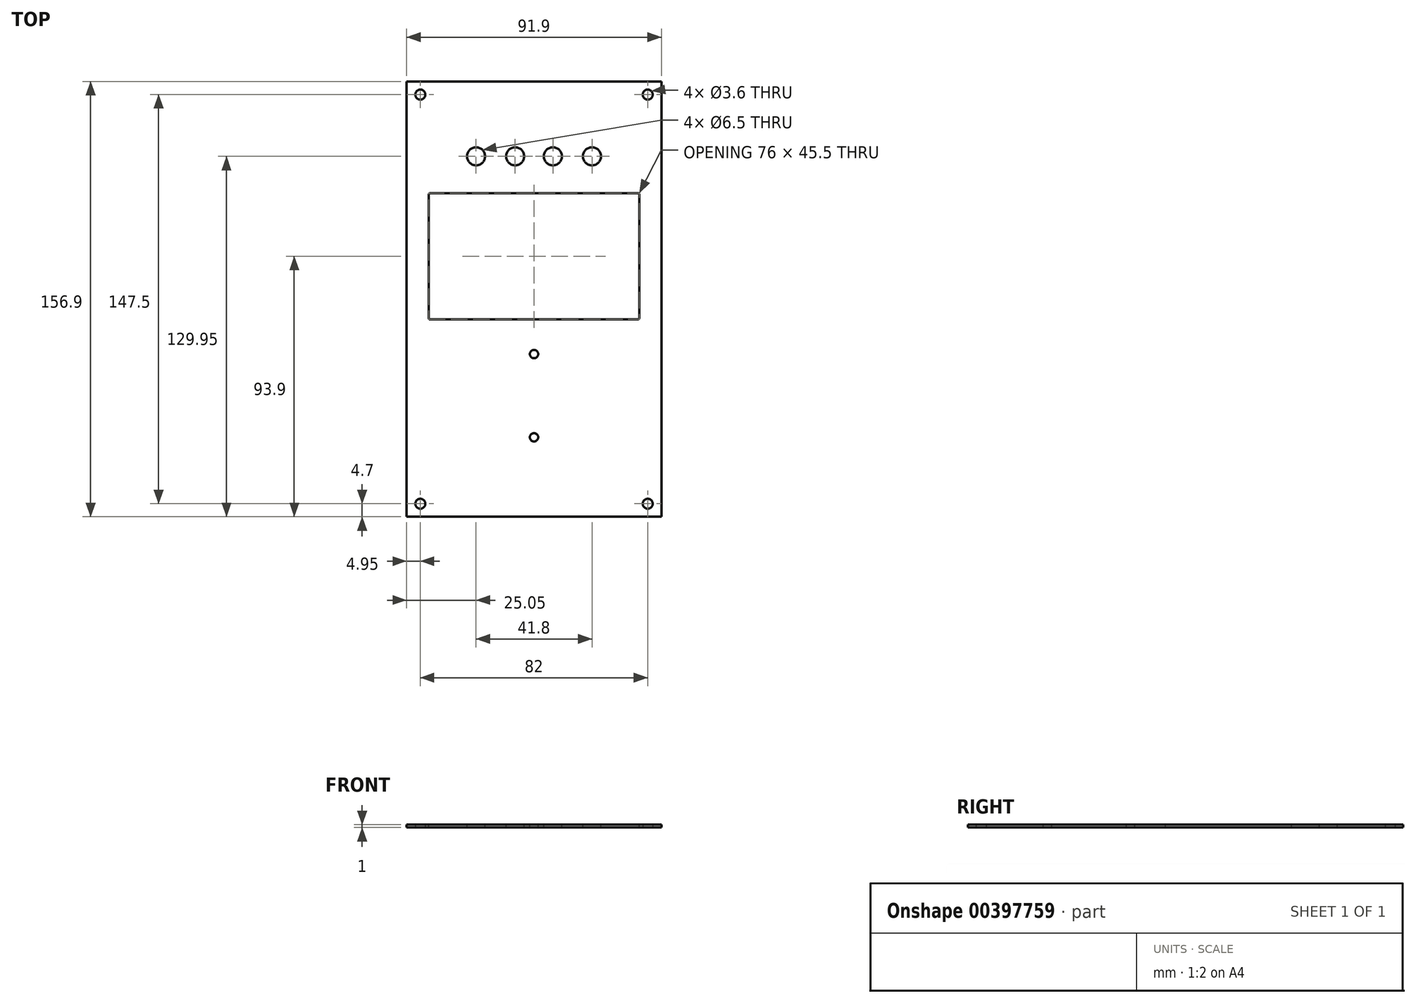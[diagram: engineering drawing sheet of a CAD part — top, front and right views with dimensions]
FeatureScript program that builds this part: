
annotation { "Feature Type Name" : "Feature", "Feature Type Description" : "" }
export const myFeature = defineFeature(function(context is Context, id is Id, definition is map)
    precondition{}
    {
        {
            var Q0;
            Q0=qCreatedBy(makeId("Top.planeOp"),FACE);
            var sketch = newSketch(context, id + "F0", { "sketchPlane" : qUnion([Q0])});
            skLineSegment(sketch, "E0.bottom", {"start": v(45.95, -78.45) * mm, "end": v(-45.95, -78.45) * mm});
            skLineSegment(sketch, "E0.top", {"start": v(45.95, 78.45) * mm, "end": v(-45.95, 78.45) * mm});
            skLineSegment(sketch, "E0.left", {"start": v(45.95, -78.45) * mm, "end": v(45.95, 78.45) * mm});
            skLineSegment(sketch, "E0.right", {"start": v(-45.95, -78.45) * mm, "end": v(-45.95, 78.45) * mm});
            skPoint(sketch, "E0.middle", {"position": v(0, 0) * mm});
            skCircle(sketch, "E1", {"center": v(-41, 73.75) * mm, "radius": 1.8 * mm});
            skCircle(sketch, "E2", {"center": v(41, 73.75) * mm, "radius": 1.8 * mm});
            skCircle(sketch, "E3", {"center": v(41, -73.75) * mm, "radius": 1.8 * mm});
            skCircle(sketch, "E4", {"center": v(-41, -73.75) * mm, "radius": 1.8 * mm});
            skSolve(sketch);
        }
        {
            var Q0;
            Q0 = qSketchRegion(id + "F0", true);
            extrude(context, id + "F1", {"entities" : qUnion([Q0]), "depth" : 1 * mm});
        }
        {
            var Q0;
            Q0=makeQuery(id+"F1.opExtrude","CAP_FACE",FACE,{"disambiguationData":[OSD([sQuery(id+"F0.wireOp",EDGE,"E0.bottom"),sQuery(id+"F0.wireOp",EDGE,"E0.top"),sQuery(id+"F0.wireOp",EDGE,"E0.left"),sQuery(id+"F0.wireOp",EDGE,"E0.right"),sQuery(id+"F0.wireOp",EDGE,"E1"),sQuery(id+"F0.wireOp",EDGE,"E2"),sQuery(id+"F0.wireOp",EDGE,"E3"),sQuery(id+"F0.wireOp",EDGE,"E4")])],"isStart":false});
            var sketch = newSketch(context, id + "F2", { "sketchPlane" : qUnion([Q0])});
            skPoint(sketch, "E5.middle", {"position": v(0, 0) * mm});
            skCircle(sketch, "E6", {"center": v(-20.9, 51.5) * mm, "radius": 3.25 * mm});
            skCircle(sketch, "E7.1.0.0", {"center": v(-6.8, 51.5) * mm, "radius": 3.25 * mm});
            skCircle(sketch, "E7.2.0.0", {"center": v(6.8, 51.5) * mm, "radius": 3.25 * mm});
            skCircle(sketch, "E7.3.0.0", {"center": v(20.9, 51.5) * mm, "radius": 3.25 * mm});
            skLineSegment(sketch, "E8.bottom", {"start": v(37.5, -7.3) * mm, "end": v(-37.5, -7.3) * mm});
            skLineSegment(sketch, "E8.top", {"start": v(37.5, 38.2) * mm, "end": v(-37.5, 38.2) * mm});
            skLineSegment(sketch, "E8.left", {"start": v(38, -6.8) * mm, "end": v(38, 37.7) * mm});
            skLineSegment(sketch, "E8.right", {"start": v(-38, -6.8) * mm, "end": v(-38, 37.7) * mm});
            skLineSegment(sketch, "E9.bottom", {"start": v(40, 38.95) * mm, "end": v(-40, 38.95) * mm});
            skLineSegment(sketch, "E9.top", {"start": v(40, 60.45) * mm, "end": v(-40, 60.45) * mm});
            skLineSegment(sketch, "E9.left", {"start": v(40, 38.95) * mm, "end": v(40, 60.45) * mm});
            skLineSegment(sketch, "E9.right", {"start": v(-40, 38.95) * mm, "end": v(-40, 60.45) * mm});
            skArc(sketch, "E10.filletArc", {"start": v(-37.5, 38.2) * mm, "mid": v(-37.85, 38.05) * mm, "end": v(-38, 37.7) * mm});
            skArc(sketch, "E11.filletArc", {"start": v(-38, -6.8) * mm, "mid": v(-37.85, -7.15) * mm, "end": v(-37.5, -7.3) * mm});
            skArc(sketch, "E12.filletArc", {"start": v(37.5, -7.3) * mm, "mid": v(37.85, -7.15) * mm, "end": v(38, -6.8) * mm});
            skArc(sketch, "E13.filletArc", {"start": v(38, 37.7) * mm, "mid": v(37.85, 38.05) * mm, "end": v(37.5, 38.2) * mm});
            skCircle(sketch, "E14", {"center": v(0, -19.8) * mm, "radius": 1.5 * mm});
            skCircle(sketch, "E15", {"center": v(0, -49.8) * mm, "radius": 1.5 * mm});
            skLineSegment(sketch, "E16.bottom", {"start": v(40.5, -61) * mm, "end": v(-40.5, -61) * mm});
            skLineSegment(sketch, "E16.top", {"start": v(40.5, 61) * mm, "end": v(-40.5, 61) * mm});
            skLineSegment(sketch, "E16.left", {"start": v(40.5, -61) * mm, "end": v(40.5, 61) * mm});
            skLineSegment(sketch, "E16.right", {"start": v(-40.5, -61) * mm, "end": v(-40.5, 61) * mm});
            skSolve(sketch);
        }
        {
            var Q0;
            Q0=makeQuery(id+"F2.imprint","IMPRINT",FACE,{"disambiguationData":[TD([[makeQuery(id+"F2.imprint","IMPRINT",EDGE,{"derivedFrom":sQuery(id+"F2.wireOp",EDGE,"E7.3.0.0")}),1.0]])]});
            var Q1;
            Q1=makeQuery(id+"F2.imprint","IMPRINT",FACE,{"disambiguationData":[TD([[makeQuery(id+"F2.imprint","IMPRINT",EDGE,{"derivedFrom":sQuery(id+"F2.wireOp",EDGE,"E6")}),1.0]])]});
            var Q2;
            Q2=makeQuery(id+"F2.imprint","IMPRINT",FACE,{"disambiguationData":[TD([[makeQuery(id+"F2.imprint","IMPRINT",EDGE,{"derivedFrom":sQuery(id+"F2.wireOp",EDGE,"E7.2.0.0")}),1.0]])]});
            var Q3;
            Q3=makeQuery(id+"F2.imprint","IMPRINT",FACE,{"disambiguationData":[TD([[makeQuery(id+"F2.imprint","IMPRINT",EDGE,{"derivedFrom":sQuery(id+"F2.wireOp",EDGE,"E7.1.0.0")}),1.0]])]});
            var Q4;
            Q4=makeQuery(id+"F2.imprint","IMPRINT",FACE,{"disambiguationData":[TD([[makeQuery(id+"F2.imprint","IMPRINT",EDGE,{"derivedFrom":sQuery(id+"F2.wireOp",EDGE,"E8.bottom")}),-1.0]])]});
            var Q5;
            Q5=makeQuery(id+"F2.imprint","IMPRINT",FACE,{"disambiguationData":[TD([[makeQuery(id+"F2.imprint","IMPRINT",EDGE,{"derivedFrom":sQuery(id+"F2.wireOp",EDGE,"E14")}),1.0]])]});
            var Q6;
            Q6=makeQuery(id+"F2.imprint","IMPRINT",FACE,{"disambiguationData":[TD([[makeQuery(id+"F2.imprint","IMPRINT",EDGE,{"derivedFrom":sQuery(id+"F2.wireOp",EDGE,"E15")}),1.0]])]});
            extrude(context, id + "F3", {"entities" : qUnion([Q0, Q1, Q2, Q3, Q4, Q5, Q6]), "operationType" : NewBodyOperationType.REMOVE, "oppositeDirection" : true, "depth" : 2 * mm});
        }
    });
